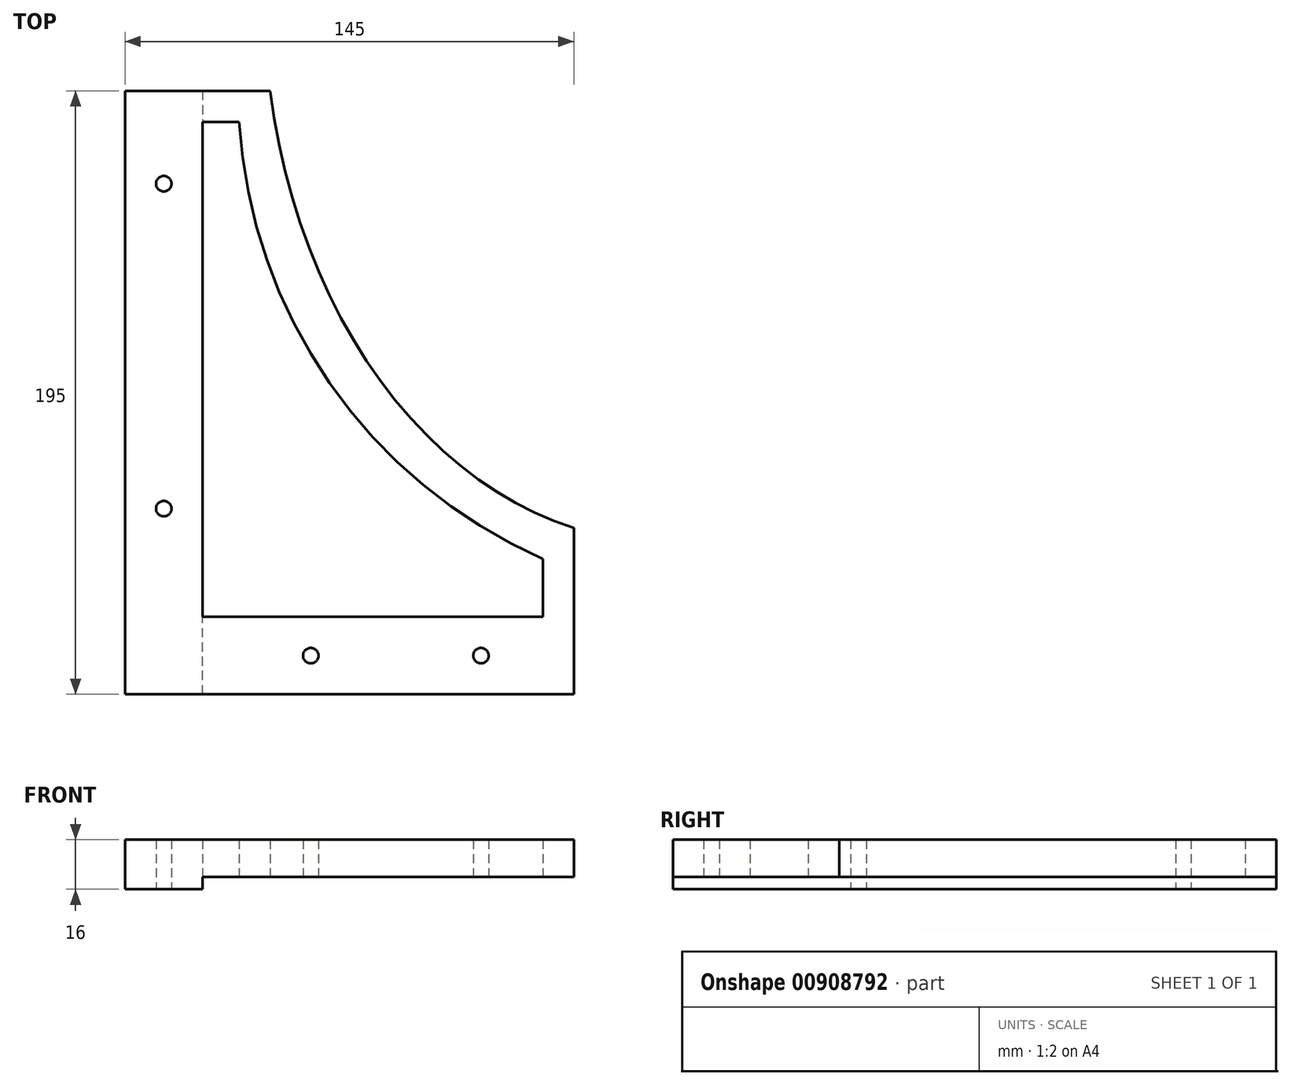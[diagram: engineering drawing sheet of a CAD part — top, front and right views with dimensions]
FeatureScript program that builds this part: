
annotation { "Feature Type Name" : "Feature", "Feature Type Description" : "" }
export const myFeature = defineFeature(function(context is Context, id is Id, definition is map)
    precondition{}
    {
        {
            var Q0;
            Q0=qCreatedBy(makeId("Top.planeOp"),FACE);
            var sketch = newSketch(context, id + "F0", { "sketchPlane" : qUnion([Q0])});
            skEllipticalArc(sketch, "E0", {});
            skLineSegment(sketch, "E1", {"start": v(-130, 0) * mm, "end": v(-130, -176) * mm});
            skPoint(sketch, "E1.endSnap0", {"position": v(0, -176) * mm});
            skLineSegment(sketch, "E2", {"start": v(-130, -176) * mm, "end": v(0, -176) * mm});
            skLineSegment(sketch, "E3", {"start": v(-130, 0) * mm, "end": v(-150, 0) * mm});
            skLineSegment(sketch, "E4", {"start": v(-150, 0) * mm, "end": v(-150, -200) * mm});
            skLineSegment(sketch, "E5", {"start": v(-150, -200) * mm, "end": v(0, -200) * mm});
            skLineSegment(sketch, "E6", {"start": v(0, -200) * mm, "end": v(0, -176) * mm});
            const initialGuessF0  = {"E0": [0, 0, 1, 0, 0.13, 0.176, 3.141592653589793, 4.71238898038469]};
            skSetInitialGuess(sketch, initialGuessF0);
            skSolve(sketch);
        }
        {
            var Q0;
            Q0=qSketchRegion(id+"F0",true);
            extrude(context, id + "F1", {"entities" : qUnion([Q0]), "depth" : 12 * mm, "offsetDistance" : 25 * mm});
        }
        {
            var Q0;
            Q0=makeQuery(id+"F1.opExtrude","SWEPT_FACE",FACE,{"disambiguationData":[OSD([sQuery(id+"F0.wireOp",EDGE,"E5")])]});
            var sketch = newSketch(context, id + "F2", { "sketchPlane" : qUnion([Q0])});
            skLineSegment(sketch, "E7.bottom", {"start": v(-150, 16) * mm, "end": v(0, 16) * mm});
            skLineSegment(sketch, "E7.top", {"start": v(-150, -4) * mm, "end": v(0, -4) * mm});
            skLineSegment(sketch, "E7.left", {"start": v(-150, 16) * mm, "end": v(-150, -4) * mm});
            skLineSegment(sketch, "E7.right", {"start": v(0, 16) * mm, "end": v(0, -4) * mm});
            skSolve(sketch);
        }
        {
            var Q0;
            Q0=qSketchRegion(id+"F2",true);
            extrude(context, id + "F3", {"entities" : qUnion([Q0]), "operationType" : NewBodyOperationType.ADD, "depth" : 5 * mm, "offsetDistance" : 25 * mm});
        }
        {
            var Q0;
            Q0=makeQuery(id+"F3.boolean.opBoolean","MERGE",FACE,{"derivedFrom":[makeQuery(id+"F1.opExtrude","SWEPT_FACE",FACE,{"disambiguationData":[OSD([sQuery(id+"F0.wireOp",EDGE,"E4")])]}),makeQuery(id+"F3.opExtrude","SWEPT_FACE",FACE,{"disambiguationData":[OSD([sQuery(id+"F2.wireOp",EDGE,"E7.left")])]})]});
            var sketch = newSketch(context, id + "F4", { "sketchPlane" : qUnion([Q0])});
            skLineSegment(sketch, "E8.bottom", {"start": v(205, 16) * mm, "end": v(0, 16) * mm});
            skLineSegment(sketch, "E8.top", {"start": v(205, -4) * mm, "end": v(0, -4) * mm});
            skLineSegment(sketch, "E8.left", {"start": v(205, 16) * mm, "end": v(205, -4) * mm});
            skLineSegment(sketch, "E8.right", {"start": v(0, 16) * mm, "end": v(0, -4) * mm});
            skSolve(sketch);
        }
        {
            var Q0;
            Q0=qSketchRegion(id+"F4",true);
            extrude(context, id + "F5", {"entities" : qUnion([Q0]), "operationType" : NewBodyOperationType.ADD, "depth" : 5 * mm, "offsetDistance" : 25 * mm});
        }
        {
            var Q0;
            Q0=makeQuery(id+"F5.boolean.opBoolean","MERGE",FACE,{"derivedFrom":[makeQuery(id+"F3.opExtrude","SWEPT_FACE",FACE,{"disambiguationData":[OSD([sQuery(id+"F2.wireOp",EDGE,"E7.top")])]}),makeQuery(id+"F5.opExtrude","SWEPT_FACE",FACE,{"disambiguationData":[OSD([sQuery(id+"F4.wireOp",EDGE,"E8.top")])]})]});
            var sketch = newSketch(context, id + "F6", { "sketchPlane" : qUnion([Q0])});
            skLineSegment(sketch, "E9", {"start": v(0, 225) * mm, "end": v(-175, 225) * mm});
            skLineSegment(sketch, "E10", {"start": v(-175, 225) * mm, "end": v(-175, 0) * mm});
            skLineSegment(sketch, "E11", {"start": v(-175, 0) * mm, "end": v(-155, 0) * mm});
            skLineSegment(sketch, "E12", {"start": v(-155, 0) * mm, "end": v(-155, 205) * mm});
            skLineSegment(sketch, "E13", {"start": v(-155, 205) * mm, "end": v(0, 205) * mm});
            skLineSegment(sketch, "E14", {"start": v(0, 205) * mm, "end": v(0, 225) * mm});
            skCircle(sketch, "E15", {"center": v(-162.5, 60) * mm, "radius": 2.5 * mm});
            skCircle(sketch, "E16", {"center": v(-162.5, 165) * mm, "radius": 2.5 * mm});
            skCircle(sketch, "E17", {"center": v(-115, 212.5) * mm, "radius": 2.5 * mm});
            skCircle(sketch, "E18", {"center": v(-60, 212.5) * mm, "radius": 2.5 * mm});
            skSolve(sketch);
        }
        {
            var Q0;
            Q0=qSketchRegion(id+"F6",true);
            extrude(context, id + "F7", {"entities" : qUnion([Q0]), "operationType" : NewBodyOperationType.ADD, "oppositeDirection" : true, "depth" : 25 * mm, "offsetDistance" : 25 * mm});
        }
        {
            var Q0;
            Q0=makeQuery(id+"F5.boolean.opBoolean","MERGE",FACE,{"derivedFrom":[makeQuery(id+"F3.opExtrude","SWEPT_FACE",FACE,{"disambiguationData":[OSD([sQuery(id+"F2.wireOp",EDGE,"E7.bottom")])]}),makeQuery(id+"F5.opExtrude","SWEPT_FACE",FACE,{"disambiguationData":[OSD([sQuery(id+"F4.wireOp",EDGE,"E8.bottom")])]})]});
            var sketch = newSketch(context, id + "F8", { "sketchPlane" : qUnion([Q0])});
            skLineSegment(sketch, "E19", {"start": v(-155, 0) * mm, "end": v(-140, 0) * mm});
            skLineSegment(sketch, "E20", {"start": v(-140, 0) * mm, "end": v(-140, -190) * mm});
            skLineSegment(sketch, "E21", {"start": v(-140, -190) * mm, "end": v(0, -190) * mm});
            skLineSegment(sketch, "E22", {"start": v(0, -190) * mm, "end": v(0, -205) * mm});
            skLineSegment(sketch, "E23", {"start": v(0, -205) * mm, "end": v(-155, -205) * mm});
            skLineSegment(sketch, "E24", {"start": v(-155, -205) * mm, "end": v(-155, 0) * mm});
            skSolve(sketch);
        }
        {
            var Q0;
            Q0=qSketchRegion(id+"F8",true);
            extrude(context, id + "F9", {"entities" : qUnion([Q0]), "operationType" : NewBodyOperationType.ADD, "depth" : 5 * mm, "offsetDistance" : 25 * mm});
        }
        {
            var Q0;
            Q0=qCreatedBy(makeId("Top.planeOp"),FACE);
            var sketch = newSketch(context, id + "F10", { "sketchPlane" : qUnion([Q0])});
            skLineSegment(sketch, "E25.bottom", {"start": v(0, 0) * mm, "end": v(-175, 0) * mm});
            skLineSegment(sketch, "E25.top", {"start": v(0, -30) * mm, "end": v(-175, -30) * mm});
            skLineSegment(sketch, "E25.left", {"start": v(0, 0) * mm, "end": v(0, -30) * mm});
            skLineSegment(sketch, "E25.right", {"start": v(-175, 0) * mm, "end": v(-175, -30) * mm});
            skLineSegment(sketch, "E26.bottom", {"start": v(0, 0) * mm, "end": v(-30, 0) * mm});
            skLineSegment(sketch, "E26.top", {"start": v(0, -225) * mm, "end": v(-30, -225) * mm});
            skLineSegment(sketch, "E26.left", {"start": v(0, 0) * mm, "end": v(0, -225) * mm});
            skLineSegment(sketch, "E26.right", {"start": v(-30, 0) * mm, "end": v(-30, -225) * mm});
            skSolve(sketch);
        }
        {
            var Q0;
            Q0=qSketchRegion(id+"F10",true);
            extrude(context, id + "F11", {"entities" : qUnion([Q0]), "operationType" : NewBodyOperationType.REMOVE, "endBound" : BoundingType.SYMMETRIC, "oppositeDirection" : true, "depth" : 50 * mm, "offsetDistance" : 25 * mm});
        }
        {
            var Q0;
            Q0=makeQuery(id+"F11.boolean.opBoolean","COPY",FACE,{"derivedFrom":makeQuery(id+"F11.opExtrude","SWEPT_FACE",FACE,{"disambiguationData":[OSD([sQuery(id+"F10.wireOp",EDGE,"E26.right")])]})});
            var sketch = newSketch(context, id + "F12", { "sketchPlane" : qUnion([Q0])});
            skLineSegment(sketch, "E27.bottom", {"start": v(-225, 21) * mm, "end": v(-30, 21) * mm});
            skLineSegment(sketch, "E27.top", {"start": v(-225, 12) * mm, "end": v(-30, 12) * mm});
            skLineSegment(sketch, "E27.left", {"start": v(-225, 21) * mm, "end": v(-225, 12) * mm});
            skLineSegment(sketch, "E27.right", {"start": v(-30, 21) * mm, "end": v(-30, 12) * mm});
            skSolve(sketch);
        }
        {
            var Q0;
            Q0=qSketchRegion(id+"F12",true);
            extrude(context, id + "F13", {"entities" : qUnion([Q0]), "operationType" : NewBodyOperationType.REMOVE, "endBound" : BoundingType.THROUGH_ALL, "oppositeDirection" : true, "depth" : 25 * mm, "offsetDistance" : 25 * mm});
        }
        {
            var Q0;
            Q0=makeQuery(id+"F1.opExtrude","CAP_FACE",FACE,{"disambiguationData":[OSD([sQuery(id+"F0.wireOp",EDGE,"E0"),sQuery(id+"F0.wireOp",EDGE,"E3"),sQuery(id+"F0.wireOp",EDGE,"E4"),sQuery(id+"F0.wireOp",EDGE,"E5"),sQuery(id+"F0.wireOp",EDGE,"E6")])],"isStart":true});
            var sketch = newSketch(context, id + "F14", { "sketchPlane" : qUnion([Q0])});
            skLineSegment(sketch, "E28", {"start": v(-40, 181.25) * mm, "end": v(-40, 200) * mm});
            skLineSegment(sketch, "E29", {"start": v(-40, 200) * mm, "end": v(-150, 200) * mm});
            skLineSegment(sketch, "E30", {"start": v(-150, 200) * mm, "end": v(-150, 40) * mm});
            skLineSegment(sketch, "E31", {"start": v(-150, 40) * mm, "end": v(-138.1, 40) * mm});
            skArc(sketch, "E32", {"start": v(-40, 181.25) * mm, "mid": v(-108.9, 124.42) * mm, "end": v(-138.1, 40) * mm});
            skSolve(sketch);
        }
        {
            var Q0;
            Q0=qSketchRegion(id+"F14",true);
            extrude(context, id + "F15", {"entities" : qUnion([Q0]), "operationType" : NewBodyOperationType.REMOVE, "oppositeDirection" : true, "depth" : 25 * mm, "offsetDistance" : 25 * mm});
        }
        {
            var Q0;
            {var subQ1=sQuery(id+"F2.wireOp",EDGE,"E7.top");var subQ3=sQuery(id+"F2.wireOp",EDGE,"E7.right");var subQ4=sQuery(id+"F2.wireOp",EDGE,"E7.left");Q0=makeQuery(id+"F15.boolean.opBoolean","MERGE",FACE,{"derivedFrom":[makeQuery(id+"F3.boolean.opBoolean","SPLIT",FACE,{"disambiguationData":[TD([makeQuery(id+"F3.opExtrude","SWEPT_FACE",FACE,{"disambiguationData":[OSD([subQ1])]})])],"derivedFrom":makeQuery(id+"F3.opExtrude","CAP_FACE",FACE,{"disambiguationData":[OSD([sQuery(id+"F2.wireOp",EDGE,"E7.bottom"),subQ1,subQ4,subQ3])],"isStart":true})})],"fromTools":[makeQuery(id+"F15.opExtrude","SWEPT_FACE",FACE,{"disambiguationData":[OSD([sQuery(id+"F14.wireOp",EDGE,"E29")])]})]});}
            var sketch = newSketch(context, id + "F16", { "sketchPlane" : qUnion([Q0])});
            skPoint(sketch, "E33.oppositeSnap0", {"position": v(150, 4) * mm});
            skLineSegment(sketch, "E33.bottom", {"start": v(30, -4) * mm, "end": v(150, -4) * mm});
            skLineSegment(sketch, "E33.top", {"start": v(30, 0) * mm, "end": v(150, 0) * mm});
            skLineSegment(sketch, "E33.left", {"start": v(30, -4) * mm, "end": v(30, 0) * mm});
            skLineSegment(sketch, "E33.right", {"start": v(150, -4) * mm, "end": v(150, 0) * mm});
            skSolve(sketch);
        }
        {
            var Q0;
            Q0=makeQuery(id+"F16.imprint","IMPRINT",FACE,{"disambiguationData":[TD([[makeQuery(id+"F16.imprint","IMPRINT",EDGE,{"derivedFrom":sQuery(id+"F16.wireOp",EDGE,"E33.bottom")}),-1.0]])]});
            extrude(context, id + "F17", {"entities" : qUnion([Q0]), "operationType" : NewBodyOperationType.REMOVE, "endBound" : BoundingType.UP_TO_NEXT, "oppositeDirection" : true, "depth" : 25 * mm, "offsetDistance" : 25 * mm});
        }
    });
